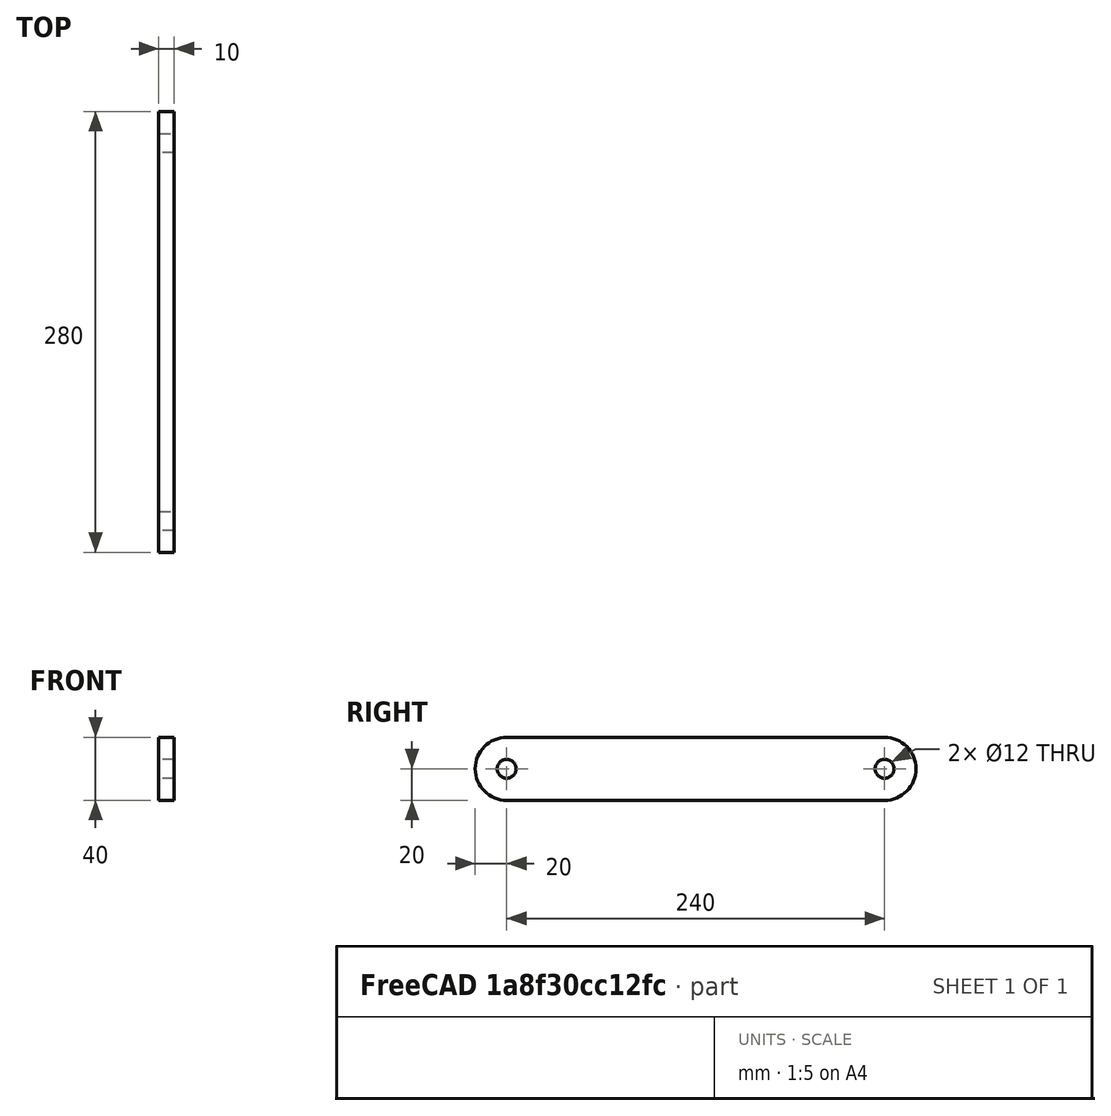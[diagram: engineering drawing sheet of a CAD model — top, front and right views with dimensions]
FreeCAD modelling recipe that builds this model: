
FCSTD DOCUMENT  (FreeCAD 0.19R24212 (Git))
Label: Bielle1
License: Creative Commons Attribution
LicenseURL: http://creativecommons.org/licenses/by/4.0/
objects: PartDesign::CoordinateSystem×1, Sketcher::SketchObject×1, PartDesign::Pad×1, PartDesign::Body×1
note: 5 computed .brp shape members not serialized (recipe doc carries the construction recipe); baked Part::Feature solids carry a one-line shape summary decoded from their .brp

FEATURE [PartDesign::CoordinateSystem] LCS_0
  AttacherType = Attacher::AttachEngine3D
  MapMode = 2
  Support = -> [X_Axis001]
FEATURE [Sketcher::SketchObject] Sketch
  FullyConstrained = true
  MapMode = 5
  Placement = pos=(0,0,0) rot=(0.57735,0.57735,0.57735;2.0944rad)
  Support = -> [YZ_Plane001]
  sketch-geometry (6):
    g0: ArcOfCircle CenterX=0 CenterY=0 CenterZ=0 NormalX=0 NormalY=0 NormalZ=1 AngleXU=0 Radius=20 StartAngle=1.5708 EndAngle=4.71239
    g1: ArcOfCircle CenterX=240 CenterY=1.4244e-12 CenterZ=0 NormalX=0 NormalY=0 NormalZ=1 AngleXU=0 Radius=20 StartAngle=4.71239 EndAngle=7.85398
    g2: LineSegment StartX=-4.03092e-11 StartY=-20 StartZ=0 EndX=240 EndY=-20 EndZ=0
    g3: LineSegment StartX=-4.01089e-11 StartY=20 StartZ=0 EndX=240 EndY=20 EndZ=0
    g4: Circle CenterX=0 CenterY=0 CenterZ=0 NormalX=0 NormalY=0 NormalZ=1 AngleXU=0 Radius=6
    g5: Circle CenterX=240 CenterY=1.4244e-12 CenterZ=0 NormalX=0 NormalY=0 NormalZ=1 AngleXU=0 Radius=6
  constraints (13):
    c: Tangent(g0,g3) = 1.5708
    c: Tangent(g0,g2) = -1.5708
    c: Tangent(g2,g1) = -1.5708
    c: Tangent(g3,g1) = 1.5708
    c: Horizontal(g2)
    c: Equal(g0,g1)
    c: Coincident(g0,g-1)
    c: Coincident(g4,g0)
    c: Coincident(g5,g1)
    c: Equal(g4,g5)
    c: Radius(g0) = 20
    c: Radius(g4) = 6
    c: DistanceX(g0,g1) = 240
FEATURE [PartDesign::Pad] Pad
  Direction = (1,1,1)
  Length = 10
  Length2 = 100
  Placement = pos=(0,0,0) rot=(0.57735,0.57735,0.57735;2.0944rad)
  Profile = -> Sketch
  Refine = true
  Type = 0
FEATURE [PartDesign::Body] Body
  Group = -> [LCS_0,Sketch,Pad]
  Origin = -> Origin001
  Tip = -> Pad
